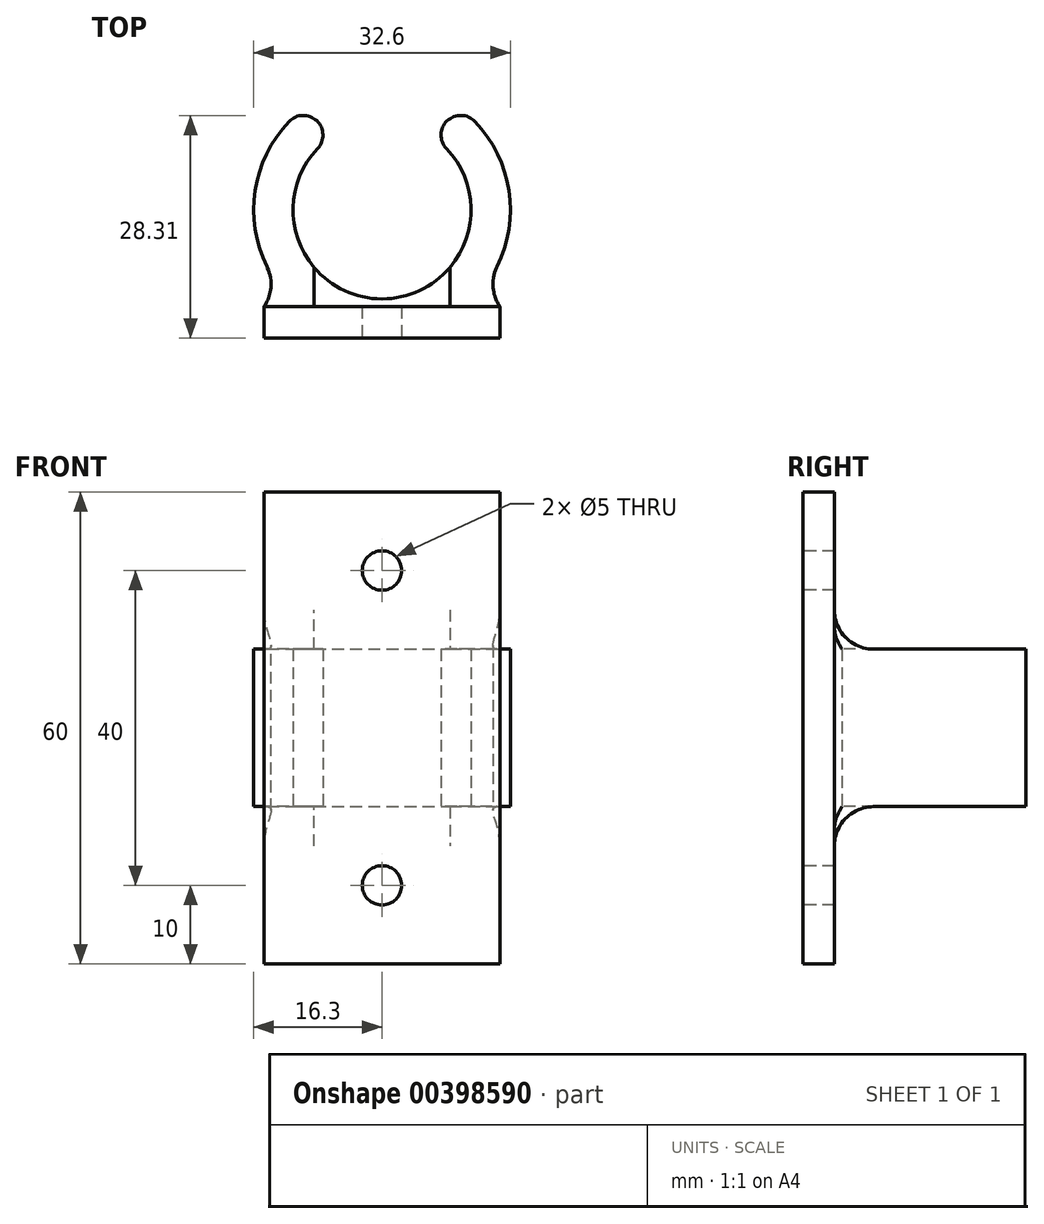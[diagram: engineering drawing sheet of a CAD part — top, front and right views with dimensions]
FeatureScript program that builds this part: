
annotation { "Feature Type Name" : "Feature", "Feature Type Description" : "" }
export const myFeature = defineFeature(function(context is Context, id is Id, definition is map)
    precondition{}
    {
        {
            var Q0;
            Q0=qCreatedBy(makeId("Top.planeOp"),FACE);
            var sketch = newSketch(context, id + "F0", { "sketchPlane" : qUnion([Q0])});
            skArc(sketch, "E0", {"start": v(-7.5, 8.45) * mm, "mid": v(0, -11.3) * mm, "end": v(7.5, 8.45) * mm});
            skArc(sketch, "E1.0", {"start": v(-7.5, 14.47) * mm, "mid": v(0, -16.3) * mm, "end": v(7.5, 14.47) * mm});
            skLineSegment(sketch, "E2", {"start": v(7.5, 8.45) * mm, "end": v(7.5, 14.47) * mm});
            skLineSegment(sketch, "E3", {"start": v(-7.5, 8.45) * mm, "end": v(-7.5, 14.47) * mm});
            skLineSegment(sketch, "E4", {"start": v(0, 0) * mm, "end": v(0, 24.12) * mm, "construction": true});
            skSolve(sketch);
        }
        {
            var Q0;
            Q0 = qSketchRegion(id + "F0", true);
            extrude(context, id + "F1", {"entities" : qUnion([Q0]), "depth" : 20 * mm});
        }
        {
            var Q0;
            Q0=makeQuery(id+"F1.opExtrude","SWEPT_EDGE",EDGE,{"disambiguationData":[OSD([sQuery(id+"F0.wireOp",EDGE,"E1.0"),sQuery(id+"F0.wireOp",EDGE,"E3")])]});
            var Q1;
            Q1=makeQuery(id+"F1.opExtrude","SWEPT_EDGE",EDGE,{"disambiguationData":[OSD([sQuery(id+"F0.wireOp",EDGE,"E1.0"),sQuery(id+"F0.wireOp",EDGE,"E2")])]});
            var Q2;
            Q2=makeQuery(id+"F1.opExtrude","SWEPT_EDGE",EDGE,{"disambiguationData":[OSD([sQuery(id+"F0.wireOp",EDGE,"E0"),sQuery(id+"F0.wireOp",EDGE,"E3")])]});
            var Q3;
            Q3=makeQuery(id+"F1.opExtrude","SWEPT_EDGE",EDGE,{"disambiguationData":[OSD([sQuery(id+"F0.wireOp",EDGE,"E0"),sQuery(id+"F0.wireOp",EDGE,"E2")])]});
            fillet(context, id + "F2", {"entities" : qUnion([Q0, Q1, Q2, Q3]), "radius" : 2.5 * mm, "tangentPropagation" : true, "allowEdgeOverflow" : false});
        }
        {
            var Q0;
            Q0=qCreatedBy(makeId("Front.planeOp"),FACE);
            cPlane(context, id + "F3", {"entities" : qUnion([Q0]), "cplaneType" : CPlaneType.OFFSET, "offset" : 16.3 * mm, "width" : 150 * mm, "height" : 150 * mm});
        }
        {
            var Q0;
            Q0=qCreatedBy(id+"F3.planeOp",FACE);
            var sketch = newSketch(context, id + "F4", { "sketchPlane" : qUnion([Q0])});
            skLineSegment(sketch, "E5.bottom", {"start": v(15, 40) * mm, "end": v(-15, 40) * mm});
            skLineSegment(sketch, "E5.top", {"start": v(15, -20) * mm, "end": v(-15, -20) * mm});
            skLineSegment(sketch, "E5.left", {"start": v(15, 40) * mm, "end": v(15, -20) * mm});
            skLineSegment(sketch, "E5.right", {"start": v(-15, 40) * mm, "end": v(-15, -20) * mm});
            skPoint(sketch, "E5.middle", {"position": v(0, 10) * mm});
            skLineSegment(sketch, "E6", {"start": v(16.3, 20) * mm, "end": v(16.3, 0) * mm, "construction": true});
            skPoint(sketch, "E7", {"position": v(16.3, 10) * mm});
            skLineSegment(sketch, "E8", {"start": v(-15, 10) * mm, "end": v(31.6, 10) * mm, "construction": true});
            skCircle(sketch, "E9", {"center": v(0, 30) * mm, "radius": 2.5 * mm});
            skCircle(sketch, "E10", {"center": v(0, -10) * mm, "radius": 2.5 * mm});
            skSolve(sketch);
        }
        {
            var Q0;
            Q0 = qSketchRegion(id + "F4", true);
            extrude(context, id + "F5", {"entities" : qUnion([Q0]), "operationType" : NewBodyOperationType.ADD, "oppositeDirection" : true, "depth" : 4 * mm});
        }
        {
            var Q0;
            Q0=makeQuery(id+"F5.boolean.opBoolean","INTERSECT",EDGE,{"disambiguationData":[OD(0.0)],"derivedFrom":[makeQuery(id+"F1.opExtrude","SWEPT_FACE",FACE,{"disambiguationData":[OSD([sQuery(id+"F0.wireOp",EDGE,"E1.0")])]}),makeQuery(id+"F5.opExtrude","CAP_FACE",FACE,{"disambiguationData":[OSD([sQuery(id+"F4.wireOp",EDGE,"E5.bottom"),sQuery(id+"F4.wireOp",EDGE,"E5.top"),sQuery(id+"F4.wireOp",EDGE,"E5.left"),sQuery(id+"F4.wireOp",EDGE,"E5.right"),sQuery(id+"F4.wireOp",EDGE,"E9"),sQuery(id+"F4.wireOp",EDGE,"E10")])],"isStart":false})]});
            var Q1;
            Q1=makeQuery(id+"F5.boolean.opBoolean","INTERSECT",EDGE,{"disambiguationData":[OD(1.0)],"derivedFrom":[makeQuery(id+"F1.opExtrude","SWEPT_FACE",FACE,{"disambiguationData":[OSD([sQuery(id+"F0.wireOp",EDGE,"E1.0")])]}),makeQuery(id+"F5.opExtrude","CAP_FACE",FACE,{"disambiguationData":[OSD([sQuery(id+"F4.wireOp",EDGE,"E5.bottom"),sQuery(id+"F4.wireOp",EDGE,"E5.top"),sQuery(id+"F4.wireOp",EDGE,"E5.left"),sQuery(id+"F4.wireOp",EDGE,"E5.right"),sQuery(id+"F4.wireOp",EDGE,"E9"),sQuery(id+"F4.wireOp",EDGE,"E10")])],"isStart":false})]});
            fillet(context, id + "F6", {"entities" : qUnion([Q0, Q1]), "radius" : 5 * mm, "tangentPropagation" : true, "allowEdgeOverflow" : false});
        }
        {
            var Q0;
            Q0=makeQuery(id+"F5.boolean.opBoolean","INTERSECT",EDGE,{"derivedFrom":[makeQuery(id+"F1.opExtrude","CAP_FACE",FACE,{"disambiguationData":[OSD([sQuery(id+"F0.wireOp",EDGE,"E0"),sQuery(id+"F0.wireOp",EDGE,"E1.0"),sQuery(id+"F0.wireOp",EDGE,"E2"),sQuery(id+"F0.wireOp",EDGE,"E3")])],"isStart":false}),makeQuery(id+"F5.opExtrude","CAP_FACE",FACE,{"disambiguationData":[OSD([sQuery(id+"F4.wireOp",EDGE,"E5.bottom"),sQuery(id+"F4.wireOp",EDGE,"E5.top"),sQuery(id+"F4.wireOp",EDGE,"E5.left"),sQuery(id+"F4.wireOp",EDGE,"E5.right"),sQuery(id+"F4.wireOp",EDGE,"E9"),sQuery(id+"F4.wireOp",EDGE,"E10")])],"isStart":false})]});
            var Q1;
            Q1=makeQuery(id+"F5.boolean.opBoolean","INTERSECT",EDGE,{"derivedFrom":[makeQuery(id+"F1.opExtrude","CAP_FACE",FACE,{"disambiguationData":[OSD([sQuery(id+"F0.wireOp",EDGE,"E0"),sQuery(id+"F0.wireOp",EDGE,"E1.0"),sQuery(id+"F0.wireOp",EDGE,"E2"),sQuery(id+"F0.wireOp",EDGE,"E3")])],"isStart":true}),makeQuery(id+"F5.opExtrude","CAP_FACE",FACE,{"disambiguationData":[OSD([sQuery(id+"F4.wireOp",EDGE,"E5.bottom"),sQuery(id+"F4.wireOp",EDGE,"E5.top"),sQuery(id+"F4.wireOp",EDGE,"E5.left"),sQuery(id+"F4.wireOp",EDGE,"E5.right"),sQuery(id+"F4.wireOp",EDGE,"E9"),sQuery(id+"F4.wireOp",EDGE,"E10")])],"isStart":false})]});
            fillet(context, id + "F7", {"entities" : qUnion([Q0, Q1]), "radius" : 5 * mm, "tangentPropagation" : true, "allowEdgeOverflow" : false});
        }
    });
